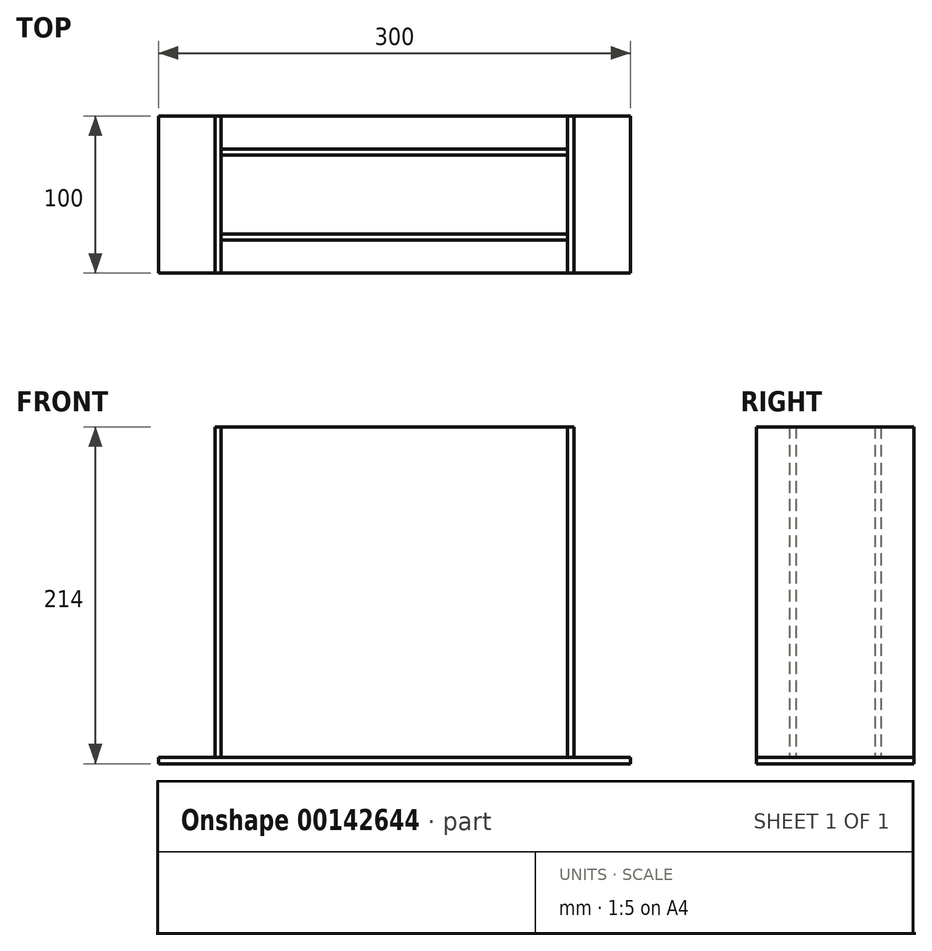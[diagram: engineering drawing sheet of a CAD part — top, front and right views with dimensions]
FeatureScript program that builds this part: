
annotation { "Feature Type Name" : "Feature", "Feature Type Description" : "" }
export const myFeature = defineFeature(function(context is Context, id is Id, definition is map)
    precondition{}
    {
        {
            var Q0;
            Q0=qCreatedBy(makeId("Top.planeOp"),FACE);
            var sketch = newSketch(context, id + "F0", { "sketchPlane" : qUnion([Q0])});
            skLineSegment(sketch, "E0.bottom", {"start": v(100, 50) * mm, "end": v(-100, 50) * mm});
            skLineSegment(sketch, "E0.top", {"start": v(100, -50) * mm, "end": v(-100, -50) * mm});
            skLineSegment(sketch, "E0.left", {"start": v(100, 50) * mm, "end": v(100, -50) * mm});
            skLineSegment(sketch, "E0.right", {"start": v(-100, 50) * mm, "end": v(-100, -50) * mm});
            skPoint(sketch, "E0.middle", {"position": v(0, 0) * mm});
            skLineSegment(sketch, "E1.bottom", {"start": v(100, -50) * mm, "end": v(150, -50) * mm});
            skLineSegment(sketch, "E1.top", {"start": v(100, 50) * mm, "end": v(150, 50) * mm});
            skLineSegment(sketch, "E1.left", {"start": v(100, -50) * mm, "end": v(100, 50) * mm});
            skLineSegment(sketch, "E1.right", {"start": v(150, -50) * mm, "end": v(150, 50) * mm});
            skLineSegment(sketch, "E2.bottom", {"start": v(-100, 50) * mm, "end": v(-150, 50) * mm});
            skLineSegment(sketch, "E2.top", {"start": v(-100, -50) * mm, "end": v(-150, -50) * mm});
            skLineSegment(sketch, "E2.right", {"start": v(-150, 50) * mm, "end": v(-150, -50) * mm});
            skSolve(sketch);
        }
        {
            assignVariable(context, id + "F1", {"name" : "plexi_thickness", "anyValue" : 4 * mm});
        }
        {
            assignVariable(context, id + "F2", {"name" : "box_height", "anyValue" : 210});
        }
        {
            var Q0;
            Q0 = qSketchRegion(id + "F0", true);
            var Q1;
            Q1=makeQuery(id+"F0.imprint","IMPRINT",FACE,{"disambiguationData":[TD([[makeQuery(id+"F0.imprint","IMPRINT",EDGE,{"derivedFrom":sQuery(id+"F0.wireOp",EDGE,"E0.bottom")}),1.0]])]});
            extrude(context, id + "F3", {"entities" : qUnion([Q0, Q1]), "depth" : getVariable(context, 'plexi_thickness')});
        }
        {
            var Q0;
            Q0=makeQuery(id+"F3.opExtrude","CAP_FACE",FACE,{"disambiguationData":[OSD([sQuery(id+"F0.wireOp",EDGE,"E0.bottom"),sQuery(id+"F0.wireOp",EDGE,"E0.top"),sQuery(id+"F0.wireOp",EDGE,"E0.left"),sQuery(id+"F0.wireOp",EDGE,"E0.right")])],"isStart":false});
            var sketch = newSketch(context, id + "F4", { "sketchPlane" : qUnion([Q0])});
            skLineSegment(sketch, "E3.bottom", {"start": v(110, 25) * mm, "end": v(-110, 25) * mm, "construction": true});
            skLineSegment(sketch, "E3.top", {"start": v(110, -25) * mm, "end": v(-110, -25) * mm, "construction": true});
            skLineSegment(sketch, "E3.left", {"start": v(110, 25) * mm, "end": v(110, -25) * mm, "construction": true});
            skLineSegment(sketch, "E3.right", {"start": v(-110, 25) * mm, "end": v(-110, -25) * mm, "construction": true});
            skPoint(sketch, "E3.middle", {"position": v(0, 0) * mm});
            skLineSegment(sketch, "E4.bottom", {"start": v(-110, -25) * mm, "end": v(110, -25) * mm});
            skLineSegment(sketch, "E4.top", {"start": v(-110, -29) * mm, "end": v(110, -29) * mm});
            skLineSegment(sketch, "E4.left", {"start": v(-110, -25) * mm, "end": v(-110, -29) * mm});
            skLineSegment(sketch, "E4.right", {"start": v(110, -25) * mm, "end": v(110, -29) * mm});
            skLineSegment(sketch, "E5.bottom", {"start": v(110, 25) * mm, "end": v(-110, 25) * mm});
            skLineSegment(sketch, "E5.top", {"start": v(110, 29) * mm, "end": v(-110, 29) * mm});
            skLineSegment(sketch, "E5.left", {"start": v(110, 25) * mm, "end": v(110, 29) * mm});
            skLineSegment(sketch, "E5.right", {"start": v(-110, 25) * mm, "end": v(-110, 29) * mm});
            skLineSegment(sketch, "E6.bottom", {"start": v(110, 50) * mm, "end": v(114, 50) * mm});
            skLineSegment(sketch, "E6.top", {"start": v(110, -50) * mm, "end": v(114, -50) * mm});
            skLineSegment(sketch, "E6.left", {"start": v(110, 50) * mm, "end": v(110, -50) * mm});
            skLineSegment(sketch, "E6.right", {"start": v(114, 50) * mm, "end": v(114, -50) * mm});
            skLineSegment(sketch, "E7.bottom", {"start": v(-110, -50) * mm, "end": v(-114, -50) * mm});
            skLineSegment(sketch, "E7.top", {"start": v(-110, 50) * mm, "end": v(-114, 50) * mm});
            skLineSegment(sketch, "E7.left", {"start": v(-110, -50) * mm, "end": v(-110, 50) * mm});
            skLineSegment(sketch, "E7.right", {"start": v(-114, -50) * mm, "end": v(-114, 50) * mm});
            skSolve(sketch);
        }
        {
            var Q0;
            {var subQ3=sQuery(id+"F4.wireOp",EDGE,"E6.bottom");Q0=makeQuery(id+"F4.imprint","IMPRINT",FACE,{"disambiguationData":[TD([[makeQuery(id+"F4.imprint","IMPRINT",EDGE,{"derivedFrom":subQ3}),-1.0]])]});}
            extrude(context, id + "F5", {"entities" : qUnion([Q0]), "depth" : (getVariable(context, 'box_height')) * mm});
        }
        {
            var Q0;
            {var subQ0=sQuery(id+"F4.wireOp",EDGE,"E4.bottom");Q0=makeQuery(id+"F4.imprint","IMPRINT",FACE,{"disambiguationData":[TD([[makeQuery(id+"F4.imprint","IMPRINT",EDGE,{"derivedFrom":subQ0}),-1.0]])]});}
            extrude(context, id + "F6", {"entities" : qUnion([Q0]), "depth" : (getVariable(context, 'box_height')) * mm});
        }
        {
            var Q0;
            {var subQ0=sQuery(id+"F4.wireOp",EDGE,"E5.bottom");Q0=makeQuery(id+"F4.imprint","IMPRINT",FACE,{"disambiguationData":[TD([[makeQuery(id+"F4.imprint","IMPRINT",EDGE,{"derivedFrom":subQ0}),-1.0]])]});}
            extrude(context, id + "F7", {"entities" : qUnion([Q0]), "depth" : (getVariable(context, 'box_height')) * mm});
        }
        {
            var Q0;
            {var subQ5=sQuery(id+"F4.wireOp",EDGE,"E7.bottom");Q0=makeQuery(id+"F4.imprint","IMPRINT",FACE,{"disambiguationData":[TD([[makeQuery(id+"F4.imprint","IMPRINT",EDGE,{"derivedFrom":subQ5}),1.0]])]});}
            extrude(context, id + "F8", {"entities" : qUnion([Q0]), "depth" : (getVariable(context, 'box_height')) * mm});
        }
    });
